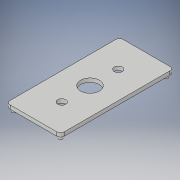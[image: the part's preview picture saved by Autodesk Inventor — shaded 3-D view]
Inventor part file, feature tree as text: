
AUTODESK INVENTOR PART (.ipt)
format: ipt  version: 2019 (Build 230136000, 136)  size: 133,632 bytes
history: native  units: mm
features: sketch x4, extrude x3, hole x1, fillet x1
ambient origin geometry x8: Origin, YZ Plane, XZ Plane, XY Plane, X Axis, Y Axis, Z Axis, Center Point
bodies: Solid1 (feature_tree)
feature tree (9):
  extrude  "Extrusion1"  Depth=60.0mm
  extrude  "Extrusion2"  Depth=10.0mm
  hole  "Hole1"  [1 undecoded]
  extrude  "Extrusion3"  Depth=2.0mm
  fillet  "Fillet1"  Radius=2.0mm
  sketch  "Sketch1"  dims[d0=2.0mm d1=0.0mm d2=60.0mm]
  sketch  "Sketch2"  dims[d3=28.763mm d4=10.0mm]
  sketch  "Sketch3"  dims[d5=2.0mm d6=0.0mm]
  sketch  "Sketch4"  dims[d7=4.305mm d8=6.0mm d9=7.087mm d10=2.0mm d11=14.3117mm d12=8.0mm d13=20.594885mm d14=1.95mm d15=2.0mm d16=2.0mm d17=2.0mm d18=2.0mm d19=2.0mm d20=0.0mm d21=2.0mm]
note: 1 required parameter value undecoded (feature->parameter linkage not recoverable at this tier; creation-order binding heuristic only, values carry confidence <= 0.55)
